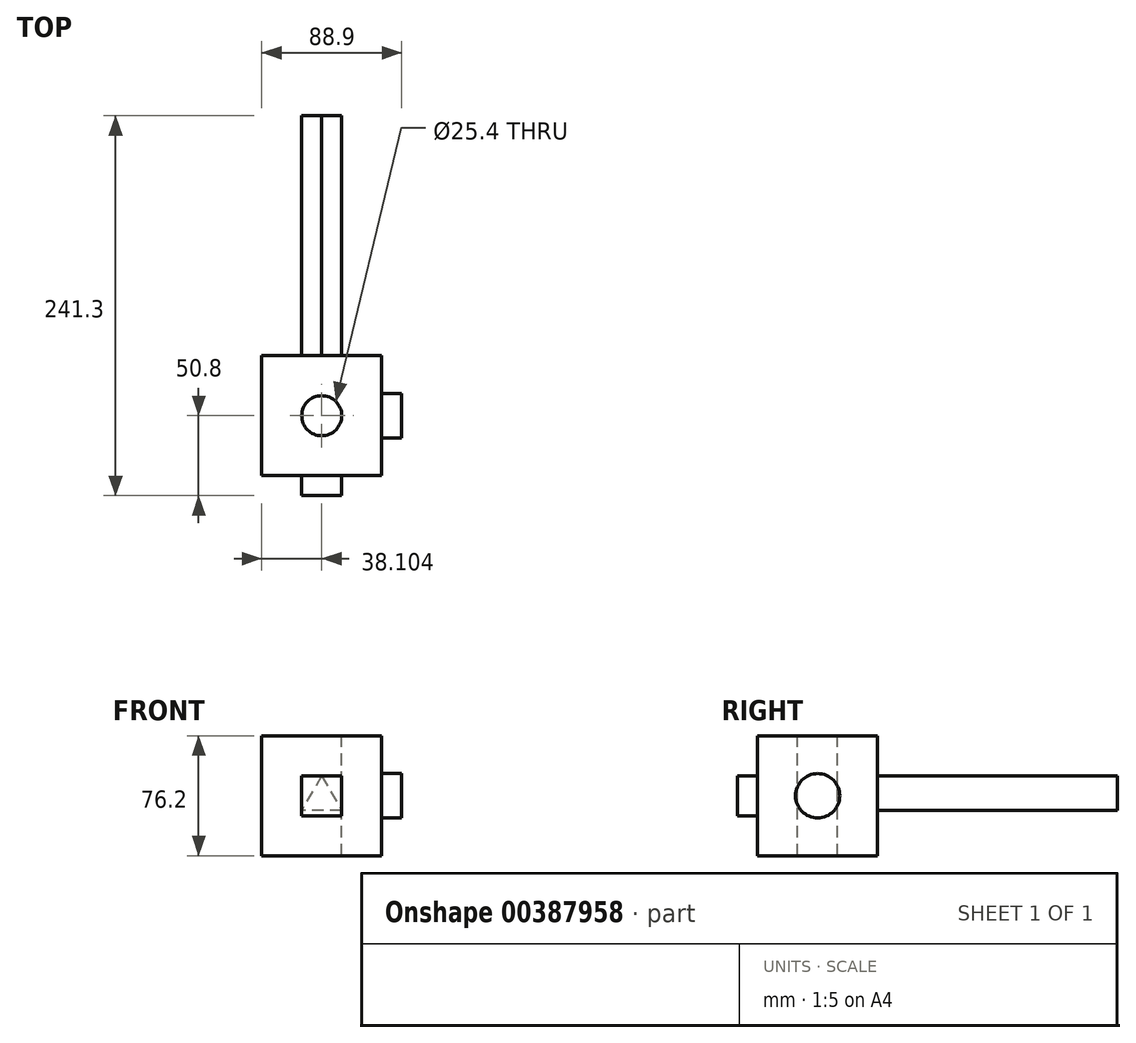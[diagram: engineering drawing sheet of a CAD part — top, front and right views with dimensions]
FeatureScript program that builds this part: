
annotation { "Feature Type Name" : "Feature", "Feature Type Description" : "" }
export const myFeature = defineFeature(function(context is Context, id is Id, definition is map)
    precondition{}
    {
        {
            var Q0;
            Q0=qCreatedBy(makeId("Front.planeOp"),FACE);
            var sketch = newSketch(context, id + "F0", { "sketchPlane" : qUnion([Q0])});
            skLineSegment(sketch, "E0.bottom", {"start": v(-40, 39.73) * mm, "end": v(36.2, 39.73) * mm});
            skLineSegment(sketch, "E0.top", {"start": v(-40, -36.47) * mm, "end": v(36.2, -36.47) * mm});
            skLineSegment(sketch, "E0.left", {"start": v(-40, 39.73) * mm, "end": v(-40, -36.47) * mm});
            skLineSegment(sketch, "E0.right", {"start": v(36.2, 39.73) * mm, "end": v(36.2, -36.47) * mm});
            skSolve(sketch);
        }
        {
            var Q0;
            Q0 = qSketchRegion(id + "F0", true);
            extrude(context, id + "F1", {"entities" : qUnion([Q0]), "depth" : 76.2 * mm});
        }
        {
            var Q0;
            Q0=makeQuery(id+"F1.opExtrude","SWEPT_FACE",FACE,{"disambiguationData":[OSD([sQuery(id+"F0.wireOp",EDGE,"E0.bottom")])]});
            var sketch = newSketch(context, id + "F2", { "sketchPlane" : qUnion([Q0])});
            skPoint(sketch, "E1", {"position": v(-1.9, -38.1) * mm});
            skSolve(sketch);
        }
        {
            var Q0;
            Q0=sQuery(id+"F2.wireOp",VERTEX,"E1");
            var Q1;
            Q1=makeQuery(id+"F1.opExtrude","SWEPT_BODY",BODY,{"disambiguationData":[OSD([sQuery(id+"F0.wireOp",EDGE,"E0.bottom"),sQuery(id+"F0.wireOp",EDGE,"E0.top"),sQuery(id+"F0.wireOp",EDGE,"E0.left"),sQuery(id+"F0.wireOp",EDGE,"E0.right")])]});
            hole(context, id + "F3", {"style" : HoleStyle.SIMPLE, "endStyle" : HoleEndStyle.THROUGH, "holeDiameter" : 25.4 * mm, "isTappedThrough" : true, "tappedDepth" : 12.7 * mm, "tapClearance" : 3, "locations" : qUnion([Q0]), "scope" : qUnion([Q1])});
        }
        {
            var Q0;
            Q0=makeQuery(id+"F1.opExtrude","CAP_FACE",FACE,{"disambiguationData":[OSD([sQuery(id+"F0.wireOp",EDGE,"E0.bottom"),sQuery(id+"F0.wireOp",EDGE,"E0.top"),sQuery(id+"F0.wireOp",EDGE,"E0.left"),sQuery(id+"F0.wireOp",EDGE,"E0.right")])],"isStart":false});
            var sketch = newSketch(context, id + "F4", { "sketchPlane" : qUnion([Q0])});
            skLineSegment(sketch, "E2.bottom", {"start": v(-14.6, 14.33) * mm, "end": v(10.8, 14.33) * mm});
            skLineSegment(sketch, "E2.top", {"start": v(-14.6, -11.07) * mm, "end": v(10.8, -11.07) * mm});
            skLineSegment(sketch, "E2.left", {"start": v(-14.6, 14.33) * mm, "end": v(-14.6, -11.07) * mm});
            skLineSegment(sketch, "E2.right", {"start": v(10.8, 14.33) * mm, "end": v(10.8, -11.07) * mm});
            skSolve(sketch);
        }
        {
            var Q0;
            Q0=makeQuery(id+"F4.imprint","IMPRINT",FACE,{"disambiguationData":[TD([[makeQuery(id+"F4.imprint","IMPRINT",EDGE,{"derivedFrom":sQuery(id+"F4.wireOp",EDGE,"E2.bottom")}),-1.0]])]});
            extrude(context, id + "F5", {"entities" : qUnion([Q0]), "operationType" : NewBodyOperationType.ADD, "depth" : 12.7 * mm});
        }
        {
            var Q0;
            Q0=makeQuery(id+"F1.opExtrude","SWEPT_FACE",FACE,{"disambiguationData":[OSD([sQuery(id+"F0.wireOp",EDGE,"E0.right")])]});
            var sketch = newSketch(context, id + "F6", { "sketchPlane" : qUnion([Q0])});
            skCircle(sketch, "E3", {"center": v(-38.1, 1.63) * mm, "radius": 14.06 * mm});
            skSolve(sketch);
        }
        {
            var Q0;
            Q0=makeQuery(id+"F6.imprint","IMPRINT",FACE,{"disambiguationData":[TD([[makeQuery(id+"F6.imprint","IMPRINT",EDGE,{"derivedFrom":sQuery(id+"F6.wireOp",EDGE,"E3")}),1.0]])]});
            extrude(context, id + "F7", {"entities" : qUnion([Q0]), "operationType" : NewBodyOperationType.ADD, "depth" : 12.7 * mm});
        }
        {
            var Q0;
            Q0=makeQuery(id+"F1.opExtrude","CAP_FACE",FACE,{"disambiguationData":[OSD([sQuery(id+"F0.wireOp",EDGE,"E0.bottom"),sQuery(id+"F0.wireOp",EDGE,"E0.top"),sQuery(id+"F0.wireOp",EDGE,"E0.left"),sQuery(id+"F0.wireOp",EDGE,"E0.right")])],"isStart":true});
            var sketch = newSketch(context, id + "F8", { "sketchPlane" : qUnion([Q0])});
            skLineSegment(sketch, "E4", {"start": v(1.9, 14.33) * mm, "end": v(-10.8, -7.67) * mm});
            skLineSegment(sketch, "E5", {"start": v(1.9, 14.33) * mm, "end": v(14.6, -7.67) * mm});
            skLineSegment(sketch, "E6", {"start": v(-10.8, -7.67) * mm, "end": v(14.6, -7.67) * mm});
            skSolve(sketch);
        }
        {
            var Q0;
            Q0=makeQuery(id+"F8.imprint","IMPRINT",FACE,{"disambiguationData":[TD([[makeQuery(id+"F8.imprint","IMPRINT",EDGE,{"derivedFrom":sQuery(id+"F8.wireOp",EDGE,"E4")}),1.0]])]});
            extrude(context, id + "F9", {"entities" : qUnion([Q0]), "operationType" : NewBodyOperationType.ADD, "depth" : 152.4 * mm});
        }
    });
